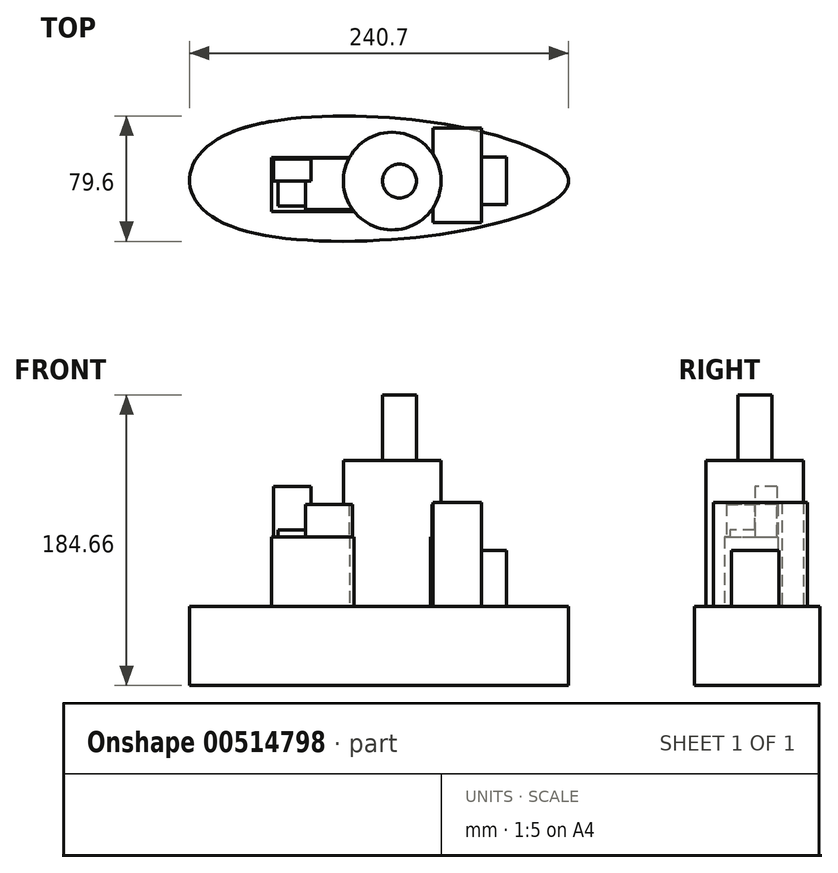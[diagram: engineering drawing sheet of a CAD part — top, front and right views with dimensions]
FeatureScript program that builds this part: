
annotation { "Feature Type Name" : "Feature", "Feature Type Description" : "" }
export const myFeature = defineFeature(function(context is Context, id is Id, definition is map)
    precondition{}
    {
        {
            var Q0;
            Q0=qCreatedBy(makeId("Top.planeOp"),FACE);
            var sketch = newSketch(context, id + "F0", { "sketchPlane" : qUnion([Q0])});
            skLineSegment(sketch, "E0.bottom", {"start": v(32.74, 30.9) * mm, "end": v(-128.34, 30.9) * mm});
            skLineSegment(sketch, "E0.top", {"start": v(32.74, -28.74) * mm, "end": v(-128.34, -28.74) * mm});
            skLineSegment(sketch, "E0.left", {"start": v(32.74, 30.9) * mm, "end": v(32.74, -28.74) * mm});
            skLineSegment(sketch, "E0.right", {"start": v(-128.34, 30.9) * mm, "end": v(-128.34, -28.74) * mm});
            skLineSegment(sketch, "E1.bottom", {"start": v(32.74, -28.74) * mm, "end": v(32.74, -28.74) * mm});
            skLineSegment(sketch, "E1.top", {"start": v(32.74, 30.9) * mm, "end": v(32.74, 30.9) * mm});
            skLineSegment(sketch, "E1.left", {"start": v(32.74, -28.74) * mm, "end": v(32.74, 30.9) * mm});
            skLineSegment(sketch, "E1.right", {"start": v(32.74, -28.74) * mm, "end": v(32.74, 30.9) * mm});
            skFitSpline(sketch, "E2", {"points": [v(32.74, 30.9) * mm, v(86.17, 0) * mm, v(32.74, -28.74) * mm, v(-128.34, -28.74) * mm, v(-154.53, 0) * mm, v(-128.34, 30.9) * mm, v(32.74, 30.9) * mm]});
            skSolve(sketch);
        }
        {
            var Q0;
            Q0 = qSketchRegion(id + "F0", true);
            extrude(context, id + "F1", {"entities" : qUnion([Q0]), "oppositeDirection" : true, "depth" : 50.3 * mm, "offsetDistance" : 25.4 * mm});
        }
        {
            var Q0;
            Q0=qCreatedBy(makeId("Top.planeOp"),FACE);
            var sketch = newSketch(context, id + "F2", { "sketchPlane" : qUnion([Q0])});
            skLineSegment(sketch, "E3.bottom", {"start": v(-102.35, -19.37) * mm, "end": v(0, -19.37) * mm});
            skLineSegment(sketch, "E3.top", {"start": v(-102.35, 14.78) * mm, "end": v(0, 14.78) * mm});
            skLineSegment(sketch, "E3.left", {"start": v(-102.35, -19.37) * mm, "end": v(-102.35, 14.78) * mm});
            skLineSegment(sketch, "E3.right", {"start": v(0, -19.37) * mm, "end": v(0, 14.78) * mm});
            skSolve(sketch);
        }
        {
            var Q0;
            Q0 = qSketchRegion(id + "F2", true);
            extrude(context, id + "F3", {"entities" : qUnion([Q0]), "operationType" : NewBodyOperationType.ADD, "depth" : 44.2 * mm, "offsetDistance" : 25.4 * mm});
        }
        {
            var Q0;
            Q0=qCreatedBy(makeId("Top.planeOp"),FACE);
            var sketch = newSketch(context, id + "F4", { "sketchPlane" : qUnion([Q0])});
            skLineSegment(sketch, "E4.bottom", {"start": v(-101.07, 14.08) * mm, "end": v(-77.33, 14.08) * mm});
            skLineSegment(sketch, "E4.top", {"start": v(-101.07, 0) * mm, "end": v(-77.33, 0) * mm});
            skLineSegment(sketch, "E4.left", {"start": v(-101.07, 14.08) * mm, "end": v(-101.07, 0) * mm});
            skLineSegment(sketch, "E4.right", {"start": v(-77.33, 14.08) * mm, "end": v(-77.33, 0) * mm});
            skSolve(sketch);
        }
        {
            var Q0;
            Q0 = qSketchRegion(id + "F4", true);
            extrude(context, id + "F5", {"entities" : qUnion([Q0]), "operationType" : NewBodyOperationType.ADD, "depth" : 76.2 * mm, "offsetDistance" : 25.4 * mm});
        }
        {
            var Q0;
            Q0=qCreatedBy(makeId("Top.planeOp"),FACE);
            var sketch = newSketch(context, id + "F6", { "sketchPlane" : qUnion([Q0])});
            skLineSegment(sketch, "E5.bottom", {"start": v(-59.8, 11.86) * mm, "end": v(-98.33, 11.86) * mm});
            skLineSegment(sketch, "E5.top", {"start": v(-59.8, -15.84) * mm, "end": v(-98.33, -15.84) * mm});
            skLineSegment(sketch, "E5.left", {"start": v(-59.8, 11.86) * mm, "end": v(-59.8, -15.84) * mm});
            skLineSegment(sketch, "E5.right", {"start": v(-98.33, 11.86) * mm, "end": v(-98.33, -15.84) * mm});
            skSolve(sketch);
        }
        {
            var Q0;
            Q0 = qSketchRegion(id + "F6", true);
            extrude(context, id + "F7", {"entities" : qUnion([Q0]), "operationType" : NewBodyOperationType.ADD, "depth" : 48.5 * mm, "offsetDistance" : 25.4 * mm});
        }
        {
            var Q0;
            Q0=qCreatedBy(makeId("Top.planeOp"),FACE);
            var sketch = newSketch(context, id + "F8", { "sketchPlane" : qUnion([Q0])});
            skLineSegment(sketch, "E6.bottom", {"start": v(0, -18.17) * mm, "end": v(-80.85, -18.17) * mm});
            skLineSegment(sketch, "E6.top", {"start": v(0, 14.67) * mm, "end": v(-80.85, 14.67) * mm});
            skLineSegment(sketch, "E6.left", {"start": v(0, -18.17) * mm, "end": v(0, 14.67) * mm});
            skLineSegment(sketch, "E6.right", {"start": v(-80.85, -18.17) * mm, "end": v(-80.85, 14.67) * mm});
            skSolve(sketch);
        }
        {
            var Q0;
            Q0 = qSketchRegion(id + "F8", true);
            extrude(context, id + "F9", {"entities" : qUnion([Q0]), "operationType" : NewBodyOperationType.ADD, "depth" : 64.77 * mm, "offsetDistance" : 25.4 * mm});
        }
        {
            var Q0;
            Q0=qCreatedBy(makeId("Top.planeOp"),FACE);
            var sketch = newSketch(context, id + "F10", { "sketchPlane" : qUnion([Q0])});
            skCircle(sketch, "E7", {"center": v(-25.84, 0) * mm, "radius": 31 * mm});
            skSolve(sketch);
        }
        {
            var Q0;
            Q0 = qSketchRegion(id + "F10", true);
            extrude(context, id + "F11", {"entities" : qUnion([Q0]), "operationType" : NewBodyOperationType.ADD, "depth" : 92.7 * mm, "offsetDistance" : 25.4 * mm});
        }
        {
            var Q0;
            Q0=qCreatedBy(makeId("Top.planeOp"),FACE);
            var sketch = newSketch(context, id + "F12", { "sketchPlane" : qUnion([Q0])});
            skCircle(sketch, "E8", {"center": v(-21.22, 0) * mm, "radius": 10.81 * mm});
            skSolve(sketch);
        }
        {
            var Q0;
            Q0 = qSketchRegion(id + "F12", true);
            extrude(context, id + "F13", {"entities" : qUnion([Q0]), "operationType" : NewBodyOperationType.ADD, "depth" : 134.37 * mm, "offsetDistance" : 25.4 * mm});
        }
        {
            var Q0;
            Q0=qCreatedBy(makeId("Top.planeOp"),FACE);
            var sketch = newSketch(context, id + "F14", { "sketchPlane" : qUnion([Q0])});
            skLineSegment(sketch, "E9.bottom", {"start": v(26.17, 15.32) * mm, "end": v(46.66, 15.32) * mm});
            skLineSegment(sketch, "E9.top", {"start": v(26.17, -14.96) * mm, "end": v(46.66, -14.96) * mm});
            skLineSegment(sketch, "E9.left", {"start": v(26.17, 15.32) * mm, "end": v(26.17, -14.96) * mm});
            skLineSegment(sketch, "E9.right", {"start": v(46.66, 15.32) * mm, "end": v(46.66, -14.96) * mm});
            skSolve(sketch);
        }
        {
            var Q0;
            Q0 = qSketchRegion(id + "F14", true);
            extrude(context, id + "F15", {"entities" : qUnion([Q0]), "operationType" : NewBodyOperationType.ADD, "depth" : 35.56 * mm, "offsetDistance" : 25.4 * mm});
        }
        {
            var Q0;
            Q0=qCreatedBy(makeId("Top.planeOp"),FACE);
            var sketch = newSketch(context, id + "F16", { "sketchPlane" : qUnion([Q0])});
            skLineSegment(sketch, "E10.bottom", {"start": v(0, 33.56) * mm, "end": v(31, 33.56) * mm});
            skLineSegment(sketch, "E10.top", {"start": v(0, -26.4) * mm, "end": v(31, -26.4) * mm});
            skLineSegment(sketch, "E10.left", {"start": v(0, 33.56) * mm, "end": v(0, -26.4) * mm});
            skLineSegment(sketch, "E10.right", {"start": v(31, 33.56) * mm, "end": v(31, -26.4) * mm});
            skSolve(sketch);
        }
        {
            var Q0;
            Q0 = qSketchRegion(id + "F16", true);
            extrude(context, id + "F17", {"entities" : qUnion([Q0]), "operationType" : NewBodyOperationType.ADD, "depth" : 66.04 * mm, "offsetDistance" : 25.4 * mm});
        }
    });
